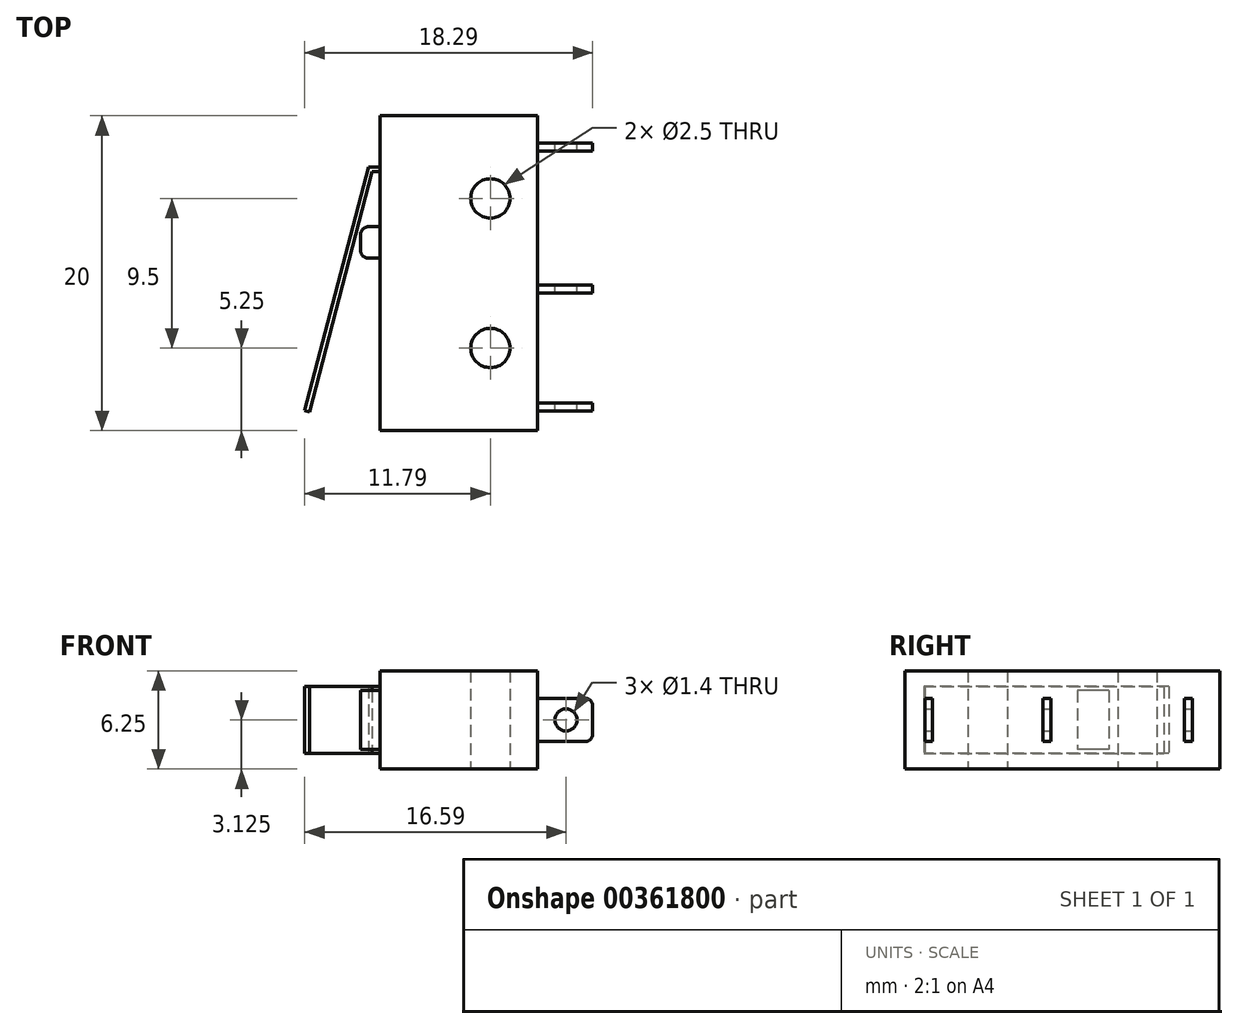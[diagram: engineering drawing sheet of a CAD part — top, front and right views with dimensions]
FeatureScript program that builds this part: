
annotation { "Feature Type Name" : "Feature", "Feature Type Description" : "" }
export const myFeature = defineFeature(function(context is Context, id is Id, definition is map)
    precondition{}
    {
        {
            var Q0;
            Q0=qCreatedBy(makeId("Top.planeOp"),FACE);
            var sketch = newSketch(context, id + "F0", { "sketchPlane" : qUnion([Q0])});
            skLineSegment(sketch, "E0.bottom", {"start": v(-5, 10) * mm, "end": v(5, 10) * mm});
            skLineSegment(sketch, "E0.top", {"start": v(-5, -10) * mm, "end": v(5, -10) * mm});
            skLineSegment(sketch, "E0.left", {"start": v(-5, 10) * mm, "end": v(-5, -10) * mm});
            skLineSegment(sketch, "E0.right", {"start": v(5, 10) * mm, "end": v(5, -10) * mm});
            skPoint(sketch, "E0.middle", {"position": v(0, 0) * mm});
            skCircle(sketch, "E1", {"center": v(2, 4.75) * mm, "radius": 1.25 * mm});
            skCircle(sketch, "E2.MirrorC", {"center": v(2, -4.75) * mm, "radius": 1.25 * mm});
            skLineSegment(sketch, "E3.bottom", {"start": v(5, 8.25) * mm, "end": v(8.5, 8.25) * mm});
            skLineSegment(sketch, "E3.top", {"start": v(5, 7.75) * mm, "end": v(8.5, 7.75) * mm});
            skLineSegment(sketch, "E3.left", {"start": v(5, 8.25) * mm, "end": v(5, 7.75) * mm});
            skLineSegment(sketch, "E3.right", {"start": v(8.5, 8.25) * mm, "end": v(8.5, 7.75) * mm});
            skLineSegment(sketch, "E4.bottom", {"start": v(5, -8.25) * mm, "end": v(8.5, -8.25) * mm});
            skLineSegment(sketch, "E4.top", {"start": v(5, -8.75) * mm, "end": v(8.5, -8.75) * mm});
            skLineSegment(sketch, "E4.left", {"start": v(5, -8.25) * mm, "end": v(5, -8.75) * mm});
            skLineSegment(sketch, "E4.right", {"start": v(8.5, -8.25) * mm, "end": v(8.5, -8.75) * mm});
            skLineSegment(sketch, "E5.bottom", {"start": v(5, -0.75) * mm, "end": v(8.5, -0.75) * mm});
            skLineSegment(sketch, "E5.top", {"start": v(5, -1.25) * mm, "end": v(8.5, -1.25) * mm});
            skLineSegment(sketch, "E5.left", {"start": v(5, -0.75) * mm, "end": v(5, -1.25) * mm});
            skLineSegment(sketch, "E5.right", {"start": v(8.5, -0.75) * mm, "end": v(8.5, -1.25) * mm});
            skLineSegment(sketch, "E6", {"start": v(-5, 6.75) * mm, "end": v(-5.73, 6.75) * mm});
            skLineSegment(sketch, "E7", {"start": v(-5.73, 6.75) * mm, "end": v(-9.8, -8.73) * mm});
            skLineSegment(sketch, "E8", {"start": v(-9.8, -8.73) * mm, "end": v(-9.5, -8.8) * mm});
            skLineSegment(sketch, "E9", {"start": v(-9.5, -8.8) * mm, "end": v(-5.5, 6.45) * mm});
            skLineSegment(sketch, "E10", {"start": v(-5.5, 6.45) * mm, "end": v(-5, 6.45) * mm});
            skLineSegment(sketch, "E11.bottom", {"start": v(-5, 2.95) * mm, "end": v(-6.25, 2.95) * mm});
            skLineSegment(sketch, "E11.top", {"start": v(-5, 0.95) * mm, "end": v(-6.25, 0.95) * mm});
            skLineSegment(sketch, "E11.left", {"start": v(-5, 2.95) * mm, "end": v(-5, 0.95) * mm});
            skLineSegment(sketch, "E11.right", {"start": v(-6.25, 2.95) * mm, "end": v(-6.25, 0.95) * mm});
            skSolve(sketch);
        }
        {
            var Q0;
            {var subQ6=sQuery(id+"F0.wireOp",EDGE,"E0.bottom");Q0=makeQuery(id+"F0.imprint","IMPRINT",FACE,{"disambiguationData":[TD([[makeQuery(id+"F0.imprint","IMPRINT",EDGE,{"derivedFrom":subQ6}),-1.0]])]});}
            extrude(context, id + "F1", {"entities" : qUnion([Q0]), "depth" : 6.25 * mm, "offsetDistance" : 25 * mm});
        }
        {
            var Q0;
            Q0=makeQuery(id+"F0.imprint","IMPRINT",FACE,{"disambiguationData":[TD([[makeQuery(id+"F0.imprint","IMPRINT",EDGE,{"derivedFrom":sQuery(id+"F0.wireOp",EDGE,"E4.bottom")}),-1.0]])]});
            var Q1;
            Q1=makeQuery(id+"F0.imprint","IMPRINT",FACE,{"disambiguationData":[TD([[makeQuery(id+"F0.imprint","IMPRINT",EDGE,{"derivedFrom":sQuery(id+"F0.wireOp",EDGE,"E5.bottom")}),-1.0]])]});
            var Q2;
            Q2=makeQuery(id+"F0.imprint","IMPRINT",FACE,{"disambiguationData":[TD([[makeQuery(id+"F0.imprint","IMPRINT",EDGE,{"derivedFrom":sQuery(id+"F0.wireOp",EDGE,"E3.bottom")}),-1.0]])]});
            var Q3;
            Q3=makeQuery(id+"F1.opExtrude","CAP_FACE",FACE,{"disambiguationData":[OSD([sQuery(id+"F0.wireOp",EDGE,"E0.bottom"),sQuery(id+"F0.wireOp",EDGE,"E0.top"),sQuery(id+"F0.wireOp",EDGE,"E0.left"),sQuery(id+"F0.wireOp",EDGE,"E0.right"),sQuery(id+"F0.wireOp",EDGE,"E1"),sQuery(id+"F0.wireOp",EDGE,"E2.MirrorC"),sQuery(id+"F0.wireOp",EDGE,"E3.left"),sQuery(id+"F0.wireOp",EDGE,"E4.left"),sQuery(id+"F0.wireOp",EDGE,"E5.left"),sQuery(id+"F0.wireOp",EDGE,"E11.left")])],"isStart":false});
            extrude(context, id + "F2", {"entities" : qUnion([Q0, Q1, Q2]), "endBound" : BoundingType.UP_TO_SURFACE, "depth" : 25 * mm, "endBoundEntityFace" : qUnion([Q3]), "hasOffset" : true, "offsetDistance" : 1.75 * mm, "hasSecondDirection" : true, "secondDirectionOppositeDirection" : false, "secondDirectionDepth" : 1.75 * mm});
        }
        {
            var Q0;
            {var subQ0=sQuery(id+"F0.wireOp",EDGE,"E6");Q0=makeQuery(id+"F0.imprint","IMPRINT",FACE,{"disambiguationData":[TD([[makeQuery(id+"F0.imprint","IMPRINT",EDGE,{"derivedFrom":subQ0}),1.0]])]});}
            var Q1;
            Q1=makeQuery(id+"F1.opExtrude","CAP_FACE",FACE,{"disambiguationData":[OSD([sQuery(id+"F0.wireOp",EDGE,"E0.bottom"),sQuery(id+"F0.wireOp",EDGE,"E0.top"),sQuery(id+"F0.wireOp",EDGE,"E0.left"),sQuery(id+"F0.wireOp",EDGE,"E0.right"),sQuery(id+"F0.wireOp",EDGE,"E1"),sQuery(id+"F0.wireOp",EDGE,"E2.MirrorC"),sQuery(id+"F0.wireOp",EDGE,"E3.left"),sQuery(id+"F0.wireOp",EDGE,"E4.left"),sQuery(id+"F0.wireOp",EDGE,"E5.left"),sQuery(id+"F0.wireOp",EDGE,"E11.left")])],"isStart":false});
            extrude(context, id + "F3", {"entities" : qUnion([Q0]), "endBound" : BoundingType.UP_TO_SURFACE, "depth" : 25 * mm, "endBoundEntityFace" : qUnion([Q1]), "hasOffset" : true, "offsetDistance" : 1 * mm, "hasSecondDirection" : true, "secondDirectionOppositeDirection" : false, "secondDirectionDepth" : 1 * mm});
        }
        {
            var Q0;
            Q0=makeQuery(id+"F0.imprint","IMPRINT",FACE,{"disambiguationData":[TD([[makeQuery(id+"F0.imprint","IMPRINT",EDGE,{"derivedFrom":sQuery(id+"F0.wireOp",EDGE,"E11.bottom")}),1.0]])]});
            var Q1;
            Q1=makeQuery(id+"F1.opExtrude","CAP_FACE",FACE,{"disambiguationData":[OSD([sQuery(id+"F0.wireOp",EDGE,"E0.bottom"),sQuery(id+"F0.wireOp",EDGE,"E0.top"),sQuery(id+"F0.wireOp",EDGE,"E0.left"),sQuery(id+"F0.wireOp",EDGE,"E0.right"),sQuery(id+"F0.wireOp",EDGE,"E1"),sQuery(id+"F0.wireOp",EDGE,"E2.MirrorC"),sQuery(id+"F0.wireOp",EDGE,"E3.left"),sQuery(id+"F0.wireOp",EDGE,"E4.left"),sQuery(id+"F0.wireOp",EDGE,"E5.left"),sQuery(id+"F0.wireOp",EDGE,"E11.left")])],"isStart":false});
            extrude(context, id + "F4", {"entities" : qUnion([Q0]), "endBound" : BoundingType.UP_TO_SURFACE, "depth" : 25 * mm, "endBoundEntityFace" : qUnion([Q1]), "hasOffset" : true, "offsetDistance" : 1.25 * mm, "hasSecondDirection" : true, "secondDirectionOppositeDirection" : false, "secondDirectionDepth" : 1.25 * mm});
        }
        {
            var Q0;
            Q0=makeQuery(id+"F4.opExtrude","SWEPT_EDGE",EDGE,{"disambiguationData":[OSD([sQuery(id+"F0.wireOp",EDGE,"E11.top"),sQuery(id+"F0.wireOp",EDGE,"E11.right")])]});
            var Q1;
            Q1=makeQuery(id+"F4.opExtrude","SWEPT_EDGE",EDGE,{"disambiguationData":[OSD([sQuery(id+"F0.wireOp",EDGE,"E11.bottom"),sQuery(id+"F0.wireOp",EDGE,"E11.right")])]});
            fillet(context, id + "F5", {"entities" : qUnion([Q0, Q1]), "radius" : .5 * mm, "tangentPropagation" : true, "allowEdgeOverflow" : false});
        }
        {
            var Q0;
            Q0=qCreatedBy(makeId("Front.planeOp"),FACE);
            var sketch = newSketch(context, id + "F6", { "sketchPlane" : qUnion([Q0])});
            skLineSegment(sketch, "E12.0", {"start": v(8.5, 4.5) * mm, "end": v(8.5, 1.75) * mm, "construction": true});
            skCircle(sketch, "E13", {"center": v(6.8, 3.12) * mm, "radius": 0.7 * mm});
            skPoint(sketch, "E13.centerSnap0", {"position": v(8.5, 3.12) * mm});
            skSolve(sketch);
        }
        {
            var Q0;
            Q0=makeQuery(id+"F6.imprint","IMPRINT",FACE,{"disambiguationData":[TD([[makeQuery(id+"F6.imprint","IMPRINT",EDGE,{"derivedFrom":sQuery(id+"F6.wireOp",EDGE,"E13")}),1.0]])]});
            extrude(context, id + "F7", {"entities" : qUnion([Q0]), "operationType" : NewBodyOperationType.REMOVE, "endBound" : BoundingType.THROUGH_ALL, "depth" : 25 * mm, "offsetDistance" : 25 * mm, "hasSecondDirection" : true, "secondDirectionBound" : SecondDirectionBoundingType.THROUGH_ALL, "secondDirectionOppositeDirection" : true, "secondDirectionDepth" : 25 * mm});
        }
        {
            var Q0;
            Q0=makeQuery(id+"F2.opExtrude","CAP_EDGE",EDGE,{"disambiguationData":[OSD([sQuery(id+"F0.wireOp",EDGE,"E4.right")])],"isStart":false});
            var Q1;
            Q1=makeQuery(id+"F2.opExtrude","CAP_EDGE",EDGE,{"disambiguationData":[OSD([sQuery(id+"F0.wireOp",EDGE,"E4.right")])],"isStart":true});
            var Q2;
            Q2=makeQuery(id+"F2.opExtrude","CAP_EDGE",EDGE,{"disambiguationData":[OSD([sQuery(id+"F0.wireOp",EDGE,"E5.right")])],"isStart":true});
            var Q3;
            Q3=makeQuery(id+"F2.opExtrude","CAP_EDGE",EDGE,{"disambiguationData":[OSD([sQuery(id+"F0.wireOp",EDGE,"E5.right")])],"isStart":false});
            var Q4;
            Q4=makeQuery(id+"F2.opExtrude","CAP_EDGE",EDGE,{"disambiguationData":[OSD([sQuery(id+"F0.wireOp",EDGE,"E3.right")])],"isStart":false});
            var Q5;
            Q5=makeQuery(id+"F2.opExtrude","CAP_EDGE",EDGE,{"disambiguationData":[OSD([sQuery(id+"F0.wireOp",EDGE,"E3.right")])],"isStart":true});
            fillet(context, id + "F8", {"entities" : qUnion([Q0, Q1, Q2, Q3, Q4, Q5]), "radius" : .5 * mm, "tangentPropagation" : true, "allowEdgeOverflow" : false});
        }
    });
